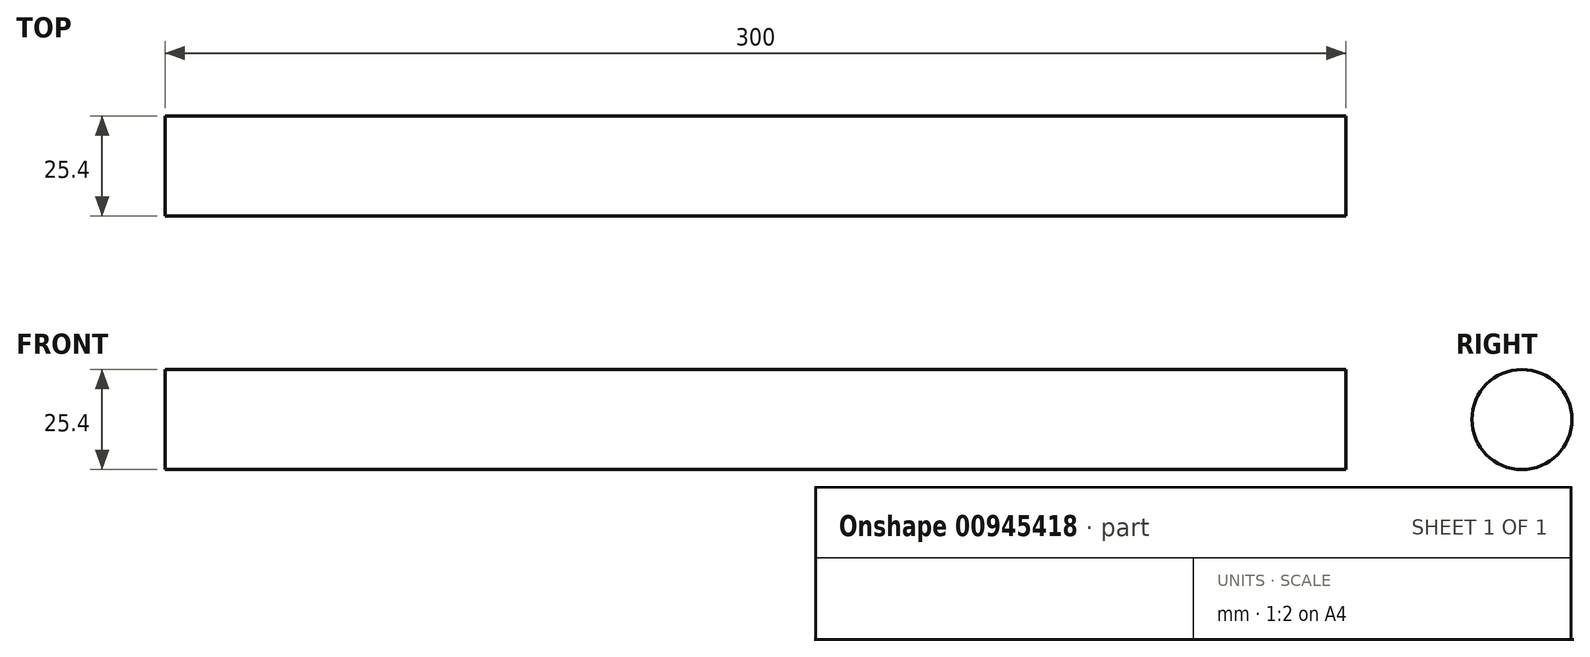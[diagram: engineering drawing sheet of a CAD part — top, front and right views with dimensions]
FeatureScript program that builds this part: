
annotation { "Feature Type Name" : "Feature", "Feature Type Description" : "" }
export const myFeature = defineFeature(function(context is Context, id is Id, definition is map)
    precondition{}
    {
        {
            var Q0;
            Q0=qCreatedBy(makeId("Right.planeOp"),FACE);
            var sketch = newSketch(context, id + "F0", { "sketchPlane" : qUnion([Q0])});
            skCircle(sketch, "E0", {"center": v(0, 0) * mm, "radius": 12.7 * mm});
            skSolve(sketch);
        }
        {
            var Q0;
            Q0=sQuery(id+"F0.wireOp",EDGE,"E0");
            extrude(context, id + "F1", {"bodyType" : ToolBodyType.SURFACE, "surfaceEntities" : qUnion([Q0]), "depth" : 300 * mm, "offsetDistance" : 25.4 * mm});
        }
    });
